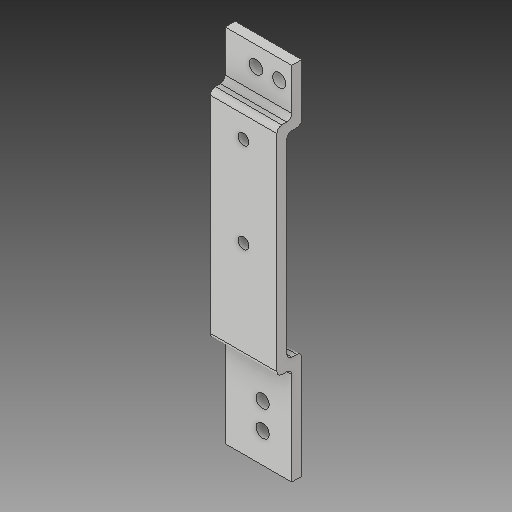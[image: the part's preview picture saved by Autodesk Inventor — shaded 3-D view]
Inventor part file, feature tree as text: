
AUTODESK INVENTOR PART (.ipt)
format: ipt  version: 2018 (Build 220112000, 112)  size: 158,208 bytes
history: native  units: mm
features: reference x9, extrude x5, sketch x5, fillet x1
ambient origin geometry x8: Origin, YZ Plane, XZ Plane, XY Plane, X Axis, Y Axis, Z Axis, Center Point
bodies: Solid1 (feature_tree)
feature tree (20):
  extrude  "Extrusion1"  Depth=130.0mm
  extrude  "Extrusion2"  Depth=6.0mm TaperAngle=0.0deg
  extrude  "Extrusion3"  Depth=6.0mm
  extrude  "Extrusion4"  Depth=34.0mm
  fillet  "Fillet1"  Radius=65.0mm
  extrude  "Extrusion5"  Depth=40.0mm
  sketch  "Sketch1"  dims[d0=40.0mm d1=130.0mm]
  sketch  "Sketch2"  dims[d2=6.0mm d3=0.0mm d4=6.0mm d5=0.0mm]
  reference  "Reference1"
  reference  "Reference2"
  sketch  "Sketch3"  dims[d6=6.0mm d7=6.0mm]
  sketch  "Sketch4"  dims[d8=3.0mm d9=0.0mm d10=34.0mm d11=65.0mm]
  sketch  "Sketch5"  dims[d12=40.0mm d13=40.0mm d14=6.0mm d15=0.0mm d16=3.0mm d17=8.0mm d18=6.0mm d19=0.0mm]
  reference  "Reference3"
  reference  "Reference4"
  reference  "Reference5"
  reference  "Reference6"
  reference  "Reference7"
  reference  "Reference8"
  reference  "Reference9"
